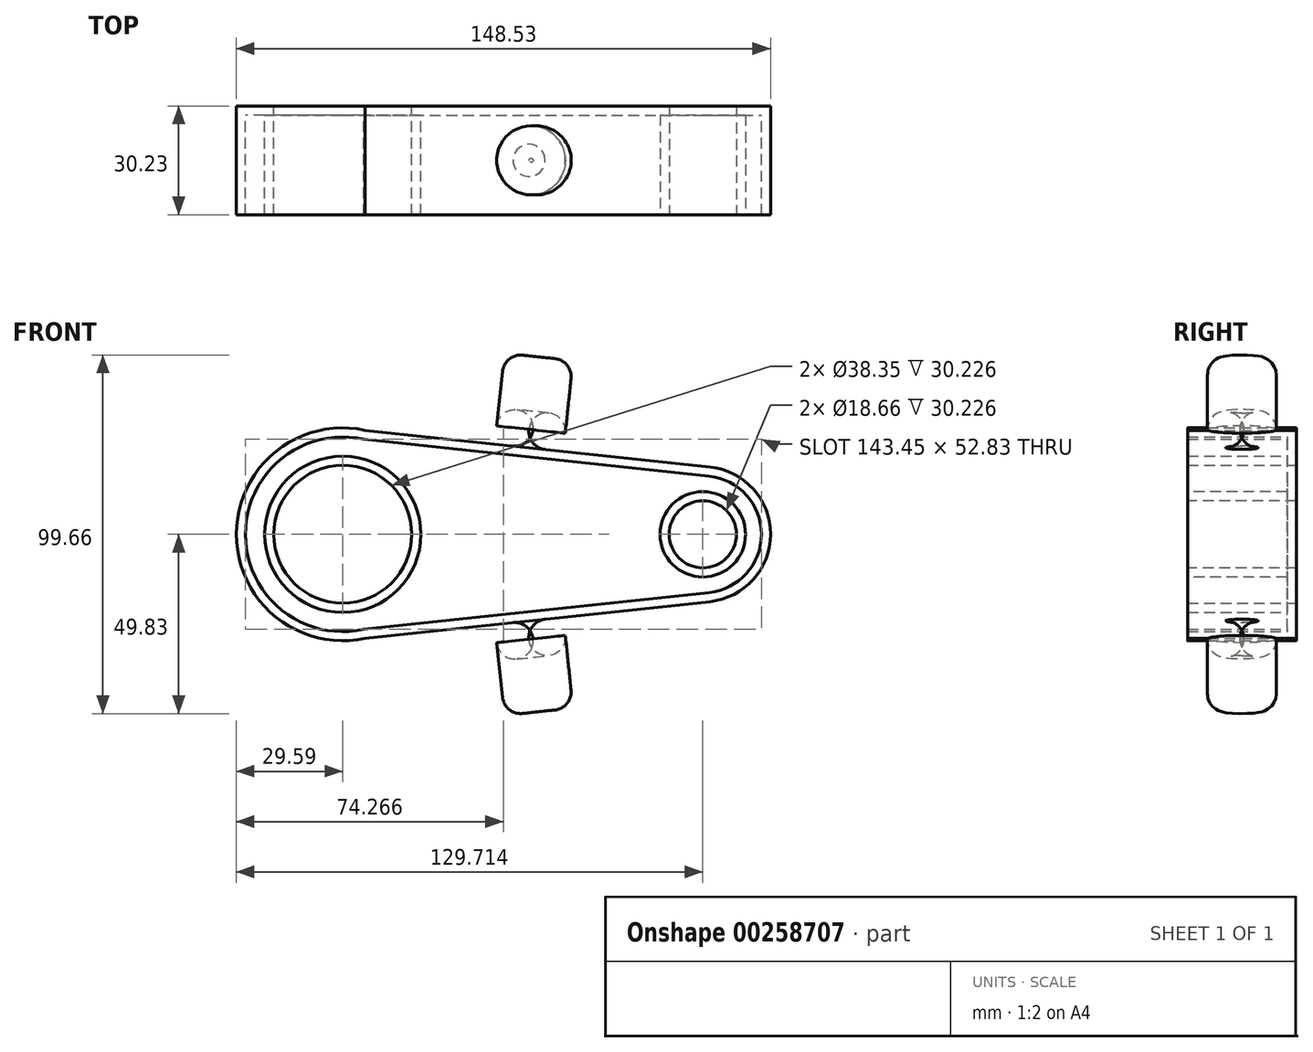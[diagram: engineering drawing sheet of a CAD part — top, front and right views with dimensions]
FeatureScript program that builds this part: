
annotation { "Feature Type Name" : "Feature", "Feature Type Description" : "" }
export const myFeature = defineFeature(function(context is Context, id is Id, definition is map)
    precondition{}
    {
        {
            var Q0;
            Q0=qCreatedBy(makeId("Front.planeOp"),FACE);
            var sketch = newSketch(context, id + "F0", { "sketchPlane" : qUnion([Q0])});
            skCircle(sketch, "E0", {"center": v(0, 0) * mm, "radius": 29.59 * mm});
            skCircle(sketch, "E1", {"center": v(100.12, 0) * mm, "radius": 18.82 * mm});
            skLineSegment(sketch, "E2", {"start": v(0, 29.59) * mm, "end": v(102.12, 18.71) * mm});
            skLineSegment(sketch, "E3", {"start": v(0, -29.59) * mm, "end": v(102.12, -18.71) * mm});
            skCircle(sketch, "E4", {"center": v(0, 0) * mm, "radius": 19.18 * mm});
            skSolve(sketch);
        }
        {
            var Q0;
            Q0 = qSketchRegion(id + "F0", true);
            extrude(context, id + "F1", {"entities" : qUnion([Q0]), "depth" : 30.23 * mm});
        }
        {
            var Q0;
            Q0=makeQuery(id+"F1.opExtrude","SWEPT_FACE",FACE,{"disambiguationData":[OSD([sQuery(id+"F0.wireOp",EDGE,"E2")])]});
            var sketch = newSketch(context, id + "F2", { "sketchPlane" : qUnion([Q0])});
            skCircle(sketch, "E5", {"center": v(48.96, -15.11) * mm, "radius": 9.59 * mm});
            skPoint(sketch, "E5.centerSnap0", {"position": v(99.56, -15.11) * mm});
            skSolve(sketch);
        }
        {
            var Q0;
            Q0 = qSketchRegion(id + "F2", true);
            extrude(context, id + "F3", {"entities" : qUnion([Q0]), "depth" : 25.4 * mm});
        }
        {
            var Q0;
            Q0=makeQuery(id+"F3.opExtrude","SWEPT_FACE",FACE,{"disambiguationData":[OSD([sQuery(id+"F2.wireOp",EDGE,"E5")])]});
            fillet(context, id + "F4", {"entities" : qUnion([Q0]), "radius" : 5.08 * mm, "tangentPropagation" : true, "allowEdgeOverflow" : false});
        }
        {
            var Q0;
            Q0=makeQuery(id+"F1.opExtrude","CAP_FACE",FACE,{"disambiguationData":[OSD([sQuery(id+"F0.wireOp",EDGE,"E0"),sQuery(id+"F0.wireOp",EDGE,"E1"),sQuery(id+"F0.wireOp",EDGE,"E2"),sQuery(id+"F0.wireOp",EDGE,"E3"),sQuery(id+"F0.wireOp",EDGE,"E4")])],"isStart":false});
            var sketch = newSketch(context, id + "F5", { "sketchPlane" : qUnion([Q0])});
            skCircle(sketch, "E6", {"center": v(100.12, 0) * mm, "radius": 9.33 * mm});
            skSolve(sketch);
        }
        {
            var Q0;
            Q0 = qSketchRegion(id + "F5", true);
            extrude(context, id + "F6", {"entities" : qUnion([Q0]), "operationType" : NewBodyOperationType.REMOVE, "oppositeDirection" : true, "depth" : 49.53 * mm});
        }
        {
            var Q0;
            Q0=makeQuery(id+"F1.opExtrude","CAP_FACE",FACE,{"disambiguationData":[OSD([sQuery(id+"F0.wireOp",EDGE,"E0"),sQuery(id+"F0.wireOp",EDGE,"E1"),sQuery(id+"F0.wireOp",EDGE,"E2"),sQuery(id+"F0.wireOp",EDGE,"E3"),sQuery(id+"F0.wireOp",EDGE,"E4")])],"isStart":false});
            shell(context, id + "F7", {"entities" : qUnion([Q0]), "thickness" : 2.54 * mm});
        }
        {
            var Q0;
            Q0=makeQuery(id+"F3.opExtrude","SWEPT_BODY",BODY,{"disambiguationData":[OSD([sQuery(id+"F2.wireOp",EDGE,"E5")])]});
            var Q1;
            Q1=makeQuery(id+"F1.opExtrude","SWEPT_BODY",BODY,{"disambiguationData":[OSD([sQuery(id+"F0.wireOp",EDGE,"E0"),sQuery(id+"F0.wireOp",EDGE,"E1"),sQuery(id+"F0.wireOp",EDGE,"E2"),sQuery(id+"F0.wireOp",EDGE,"E3"),sQuery(id+"F0.wireOp",EDGE,"E4")])]});
            var Q2;
            Q2=qCreatedBy(makeId("Top.planeOp"),FACE);
            mirror(context, id + "F8", {"entities" : qUnion([Q0, Q1]), "mirrorPlane" : qUnion([Q2])});
        }
    });
